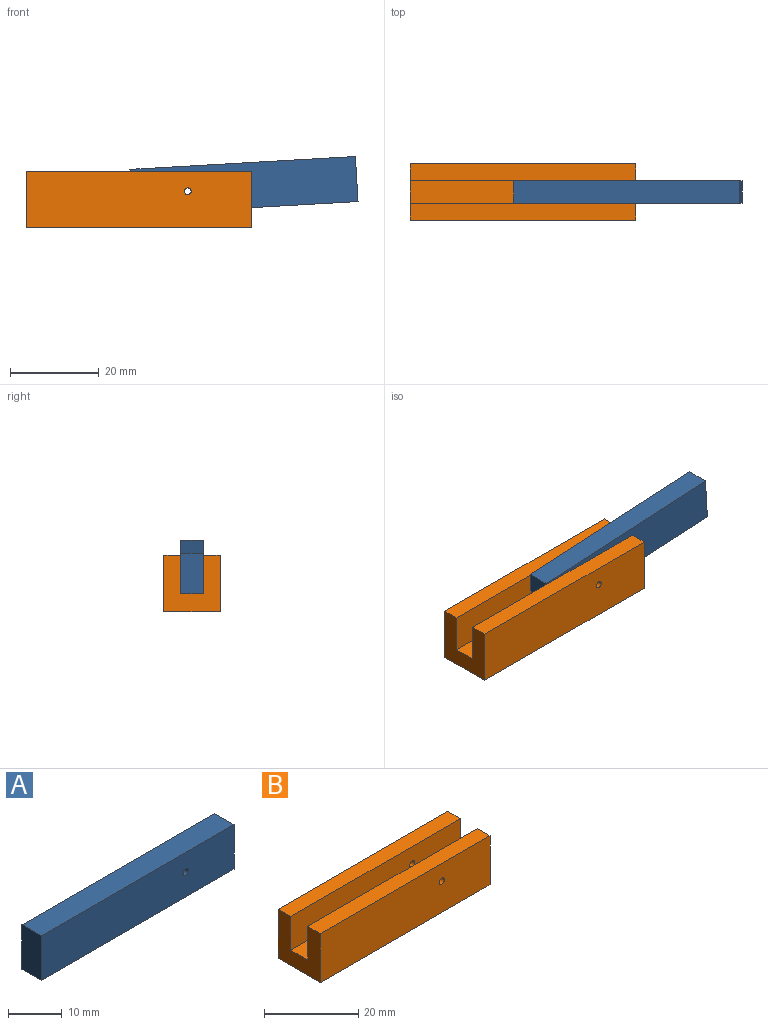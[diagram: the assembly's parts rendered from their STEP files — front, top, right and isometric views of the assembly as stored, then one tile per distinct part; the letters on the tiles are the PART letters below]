
ASSEMBLY  parts=2 mates=1
PART A: 7 faces, bbox 50.8x5.1x10.2 mm
  f0: plane 50.8x10.16mm, normal (0,-1,0), area 514.3mm2, adj f1,f3,f4,f5,f6
  f1: plane 50.8x5.08mm, normal (0,0,-1), area 258.1mm2, adj f0,f2,f4,f5
  f2: plane 50.8x10.16mm, normal (0,1,0), area 514.3mm2, adj f1,f3,f4,f5,f6
  f3: plane 50.8x5.08mm, normal (0,0,1), area 258.1mm2, adj f0,f2,f4,f5
  f4: plane 10.16x5.08mm, normal (1,0,0), area 51.6mm2, adj f0,f1,f2,f3
  f5: plane 10.16x5.08mm, normal (-1,0,0), area 51.6mm2, adj f0,f1,f2,f3
  f6: cylinder r=0.76mm len=5.08mm, axis (0,1,0), area 24.3mm2, adj f0,f2
PART B: 13 faces, bbox 50.8x12.7x12.7 mm
  f0: plane 50.8x12.7mm, normal (0,1,0), area 643.3mm2, adj f1,f7,f8,f9,f12
  f1: plane 50.8x3.81mm, normal (0,0,1), area 193.5mm2, adj f0,f2,f8,f9
  f2: plane 50.8x11.28mm, normal (0,-1,0), area 460.2mm2, adj f1,f3,f8,f9,f10,f12
  f3: plane 36.4x5.08mm, normal (0,0,1), area 184.9mm2, adj f2,f4,f8,f10
  f4: plane 50.8x11.28mm, normal (0,1,0), area 460.2mm2, adj f3,f5,f8,f9,f10,f11
  f5: plane 50.8x3.81mm, normal (0,0,1), area 193.5mm2, adj f4,f6,f8,f9
  f6: plane 50.8x12.7mm, normal (0,-1,0), area 643.3mm2, adj f5,f7,f8,f9,f11
  f7: plane 50.8x12.7mm, normal (0,0,-1), area 645.2mm2, adj f0,f6,f8,f9
  f8: plane 12.7x12.7mm, normal (-1,0,0), area 116.9mm2, adj f0,f1,f2,f3,f4,f5,f6,f7
  f9: plane 12.7x12.7mm, normal (1,0,0), area 104mm2, adj f0,f1,f2,f4,f5,f6,f7,f10
  f10: plane 14.41x5.08mm, normal (0.17,0,0.98), area 74.3mm2, adj f2,f3,f4,f9
  f11: cylinder r=0.76mm len=3.81mm, axis (0,1,0), area 18.2mm2, adj f4,f6
  f12: cylinder r=0.76mm len=3.81mm, axis (0,1,0), area 18.2mm2, adj f0,f2
PLACE A rot(axis=(0,1,0),176.7deg) t=(23.31,-2.54,9.63)mm
PLACE B at identity fixed
MATE revolute A.f6 <-> B.f11  axis (0,1,0) through (-14.41,2.54,1.8)mm
